# Revit family: RL-5 Return Valve Straight Model 3923
name_source: partatom
category: Rohrzubehör
units: mm (PartAtom-declared; Revit-internal decimal feet)

## family parameters
Arbeitsebenenbasiert = Nein
Beim Laden mit Abzugskörper schneiden = Nein
Bemaßung runder Anschluss = Durchmesser verwenden
Gemeinsam genutzt = Nein
Immer vertikal = Nein
OmniClass-Nummer = 23.65.55.14
OmniClass-Titel = Valves for Liquid Services
Teiletyp = Unterbricht

## types (1)
- RL-5 Return Valve Straight Model 3923
    Application = Hot Water Heating Systems
After installation of the return valve it is possible to close the radiator return connection.
When the intake valve is closed simultaneously (“0“-position for thermostat valves) it is possible to remove the radiator while the heating system remains under pressure.
Servicing and working behind the radiator (repapering, laying tiles) is possible without having to switch off the rest of the system.
The HERZ-RL-5 valve adjusts to allow the exact water quantity to flow through the radiator according to the heat requirements.
This is recommended particularly in systems equipped with thermostatic valves because lowering the temperature during nighttime becomes fully effective in terms of reducing power input when the water flowquantity is limited and the hydraulic equilibrium of the system is retained.
The HERZ-RL-5 valve permits filling or draining the radiator or the entire heating system.
    Body = nickel-plated
    H03 = 5 mm  [stored 0.0164042 ft]
    H05 = 9.5 mm
    H06 = 3.5 mm  [stored 0.0114829 ft]
    Hersteller = HERZ Armaturen Ges.m.b.H
    Max. operating pressure = 1000000.0 Pa
    Max. operating temperature = 110 °C
    Medium = Hot water quality according to Austrian standard ÖNORM H 5195 and/or VDI guideline 2035.
    Model = All models are nickel-plated and are universal models with special socket threaded pipe and compression union.
    R01 = 11 mm  [stored 0.0360892 ft]
    R02 = 9.75 mm  [stored 0.0319882 ft]
    R04 = 12 mm  [stored 0.0393701 ft]
    R05 = 9.75 mm  [stored 0.0319882 ft]
    S01 = 10 mm  [stored 0.0328084 ft]
    S03 = 61 mm
    S04 = 45 mm
    SCRNCODE = 05;01;02
    SCRNSEQ = ARM;ARM_TYP="ALLF";2
    URL = www.herzvalves.com
    Vorgabe-Ansicht = 0 mm  [stored 0 ft]
    W01 = 120.00°

note: [stored X ft] marks values corroborated as IEEE doubles in the binary element streams (Revit-internal decimal feet)
